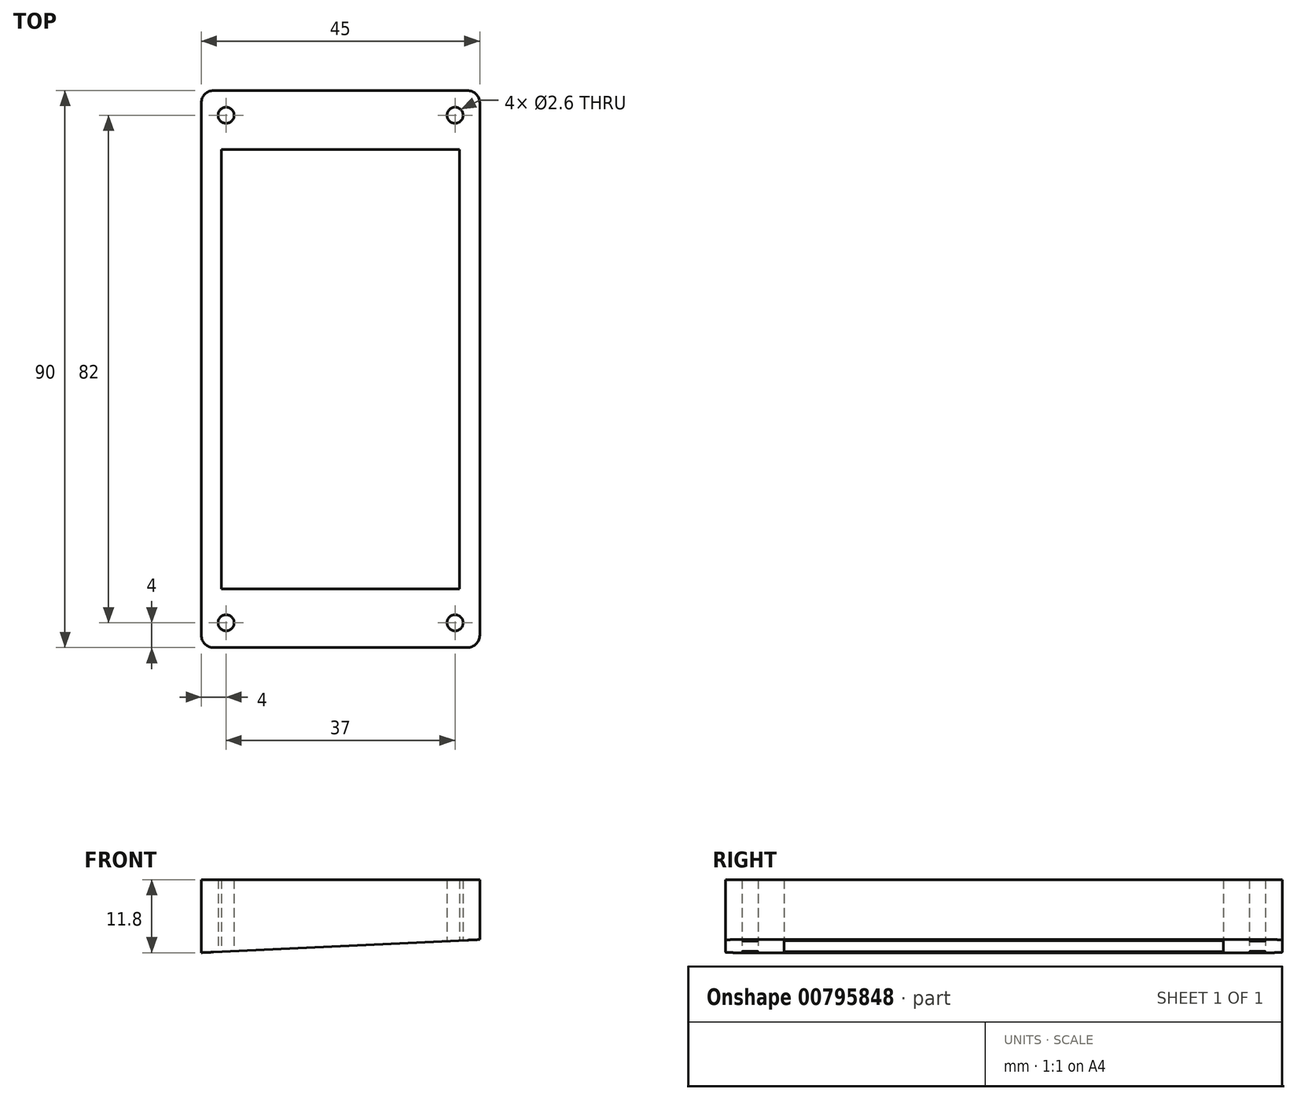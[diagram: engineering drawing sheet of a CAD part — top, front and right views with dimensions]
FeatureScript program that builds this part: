
annotation { "Feature Type Name" : "Feature", "Feature Type Description" : "" }
export const myFeature = defineFeature(function(context is Context, id is Id, definition is map)
    precondition{}
    {
        {
            var Q0;
            Q0=qCreatedBy(makeId("Top.planeOp"),FACE);
            var sketch = newSketch(context, id + "F0", { "sketchPlane" : qUnion([Q0])});
            skLineSegment(sketch, "E0.bottom", {"start": v(-20.5, 45) * mm, "end": v(20.5, 45) * mm});
            skLineSegment(sketch, "E0.top", {"start": v(-20.5, -45) * mm, "end": v(20.5, -45) * mm});
            skLineSegment(sketch, "E0.left", {"start": v(-22.5, 43) * mm, "end": v(-22.5, -43) * mm});
            skLineSegment(sketch, "E0.right", {"start": v(22.5, 43) * mm, "end": v(22.5, -43) * mm});
            skLineSegment(sketch, "E1.bottom", {"start": v(-19.25, 35.5) * mm, "end": v(19.25, 35.5) * mm});
            skLineSegment(sketch, "E1.top", {"start": v(-19.25, -35.5) * mm, "end": v(19.25, -35.5) * mm});
            skLineSegment(sketch, "E1.left", {"start": v(-19.25, 35.5) * mm, "end": v(-19.25, -35.5) * mm});
            skLineSegment(sketch, "E1.right", {"start": v(19.25, 35.5) * mm, "end": v(19.25, -35.5) * mm});
            skCircle(sketch, "E2", {"center": v(-18.5, 41) * mm, "radius": 1.3 * mm});
            skCircle(sketch, "E3.0.1.0", {"center": v(-18.5, -41) * mm, "radius": 1.3 * mm});
            skCircle(sketch, "E3.1.0.0", {"center": v(18.5, 41) * mm, "radius": 1.3 * mm});
            skCircle(sketch, "E3.1.1.0", {"center": v(18.5, -41) * mm, "radius": 1.3 * mm});
            skLineSegment(sketch, "E3.direction1", {"start": v(-18.5, 41) * mm, "end": v(18.5, 41) * mm, "construction": true});
            skLineSegment(sketch, "E3.direction2", {"start": v(-18.5, 41) * mm, "end": v(-18.5, -41) * mm, "construction": true});
            skPoint(sketch, "E4.visualSharp", {"position": v(-22.5, 45) * mm});
            skArc(sketch, "E4.filletArc", {"start": v(-20.5, 45) * mm, "mid": v(-21.91, 44.41) * mm, "end": v(-22.5, 43) * mm});
            skPoint(sketch, "E5.visualSharp", {"position": v(22.5, 45) * mm});
            skArc(sketch, "E5.filletArc", {"start": v(22.5, 43) * mm, "mid": v(21.91, 44.41) * mm, "end": v(20.5, 45) * mm});
            skPoint(sketch, "E6.visualSharp", {"position": v(-22.5, -45) * mm});
            skArc(sketch, "E6.filletArc", {"start": v(-22.5, -43) * mm, "mid": v(-21.91, -44.41) * mm, "end": v(-20.5, -45) * mm});
            skPoint(sketch, "E7.visualSharp", {"position": v(22.5, -45) * mm});
            skArc(sketch, "E7.filletArc", {"start": v(20.5, -45) * mm, "mid": v(21.91, -44.41) * mm, "end": v(22.5, -43) * mm});
            skSolve(sketch);
        }
        {
            var Q0;
            Q0 = qSketchRegion(id + "F0", true);
            extrude(context, id + "F1", {"entities" : qUnion([Q0]), "depth" : 11.8 * mm, "offsetDistance" : 25 * mm});
        }
        {
            var Q0;
            Q0=qCreatedBy(makeId("Front.planeOp"),FACE);
            var sketch = newSketch(context, id + "F2", { "sketchPlane" : qUnion([Q0])});
            skLineSegment(sketch, "E8", {"start": v(-22.5, 0) * mm, "end": v(22.5, 0) * mm});
            skLineSegment(sketch, "E9", {"start": v(22.5, 0) * mm, "end": v(22.5, 2.12) * mm});
            skLineSegment(sketch, "E10", {"start": v(22.5, 2.12) * mm, "end": v(-22.5, 0) * mm});
            skSolve(sketch);
        }
        {
            var Q0;
            Q0 = qSketchRegion(id + "F2", true);
            extrude(context, id + "F3", {"entities" : qUnion([Q0]), "operationType" : NewBodyOperationType.REMOVE, "endBound" : BoundingType.SYMMETRIC, "depth" : 400 * mm, "offsetDistance" : 25 * mm});
        }
    });
